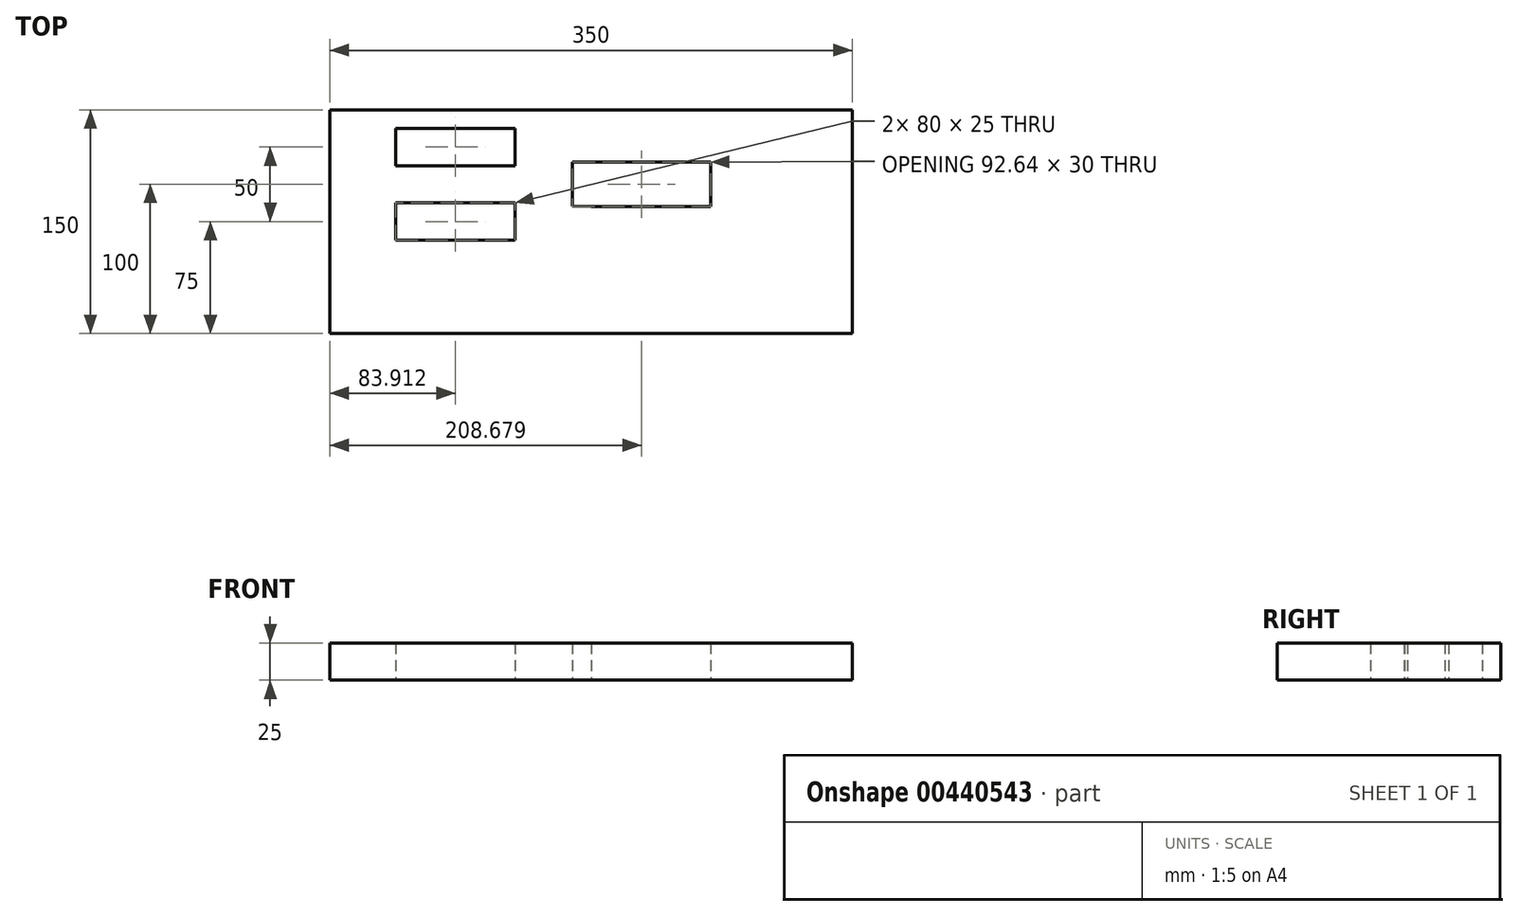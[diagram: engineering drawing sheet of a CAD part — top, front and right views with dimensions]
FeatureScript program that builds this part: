
annotation { "Feature Type Name" : "Feature", "Feature Type Description" : "" }
export const myFeature = defineFeature(function(context is Context, id is Id, definition is map)
    precondition{}
    {
        {
            var Q0;
            Q0=qCreatedBy(makeId("Top.planeOp"),FACE);
            var sketch = newSketch(context, id + "F0", { "sketchPlane" : qUnion([Q0])});
            skLineSegment(sketch, "E0.bottom", {"start": v(-175, 75) * mm, "end": v(175, 75) * mm});
            skLineSegment(sketch, "E0.top", {"start": v(-175, -75) * mm, "end": v(175, -75) * mm});
            skLineSegment(sketch, "E0.left", {"start": v(-175, 75) * mm, "end": v(-175, -75) * mm});
            skLineSegment(sketch, "E0.right", {"start": v(175, 75) * mm, "end": v(175, -75) * mm});
            skPoint(sketch, "E0.middle", {"position": v(0, 0) * mm});
            skLineSegment(sketch, "E1", {"start": v(-131.09, 62.5) * mm, "end": v(-51.09, 62.5) * mm});
            skLineSegment(sketch, "E2", {"start": v(-51.09, 37.5) * mm, "end": v(-131.09, 37.5) * mm});
            skLineSegment(sketch, "E3", {"start": v(-131.09, 12.5) * mm, "end": v(-51.09, 12.5) * mm});
            skLineSegment(sketch, "E4", {"start": v(-131.09, -12.5) * mm, "end": v(-51.09, -12.5) * mm});
            skLineSegment(sketch, "E5", {"start": v(-51.09, 62.5) * mm, "end": v(-51.09, 37.5) * mm});
            skLineSegment(sketch, "E6", {"start": v(-51.09, 12.5) * mm, "end": v(-51.09, -12.5) * mm});
            skLineSegment(sketch, "E7", {"start": v(-131.09, 12.5) * mm, "end": v(-131.09, -12.5) * mm});
            skLineSegment(sketch, "E8", {"start": v(-131.09, 37.5) * mm, "end": v(-131.09, 62.5) * mm});
            skLineSegment(sketch, "E9", {"start": v(0, -75) * mm, "end": v(80, -75) * mm});
            skLineSegment(sketch, "E10", {"start": v(80, 75) * mm, "end": v(0, 75) * mm});
            skLineSegment(sketch, "E11", {"start": v(0, 40) * mm, "end": v(80, 40) * mm});
            skLineSegment(sketch, "E12", {"start": v(80, 10) * mm, "end": v(0, 10) * mm});
            skLineSegment(sketch, "E13", {"start": v(80, 40) * mm, "end": v(80, 10) * mm});
            skLineSegment(sketch, "E14", {"start": v(0, 40) * mm, "end": v(-12.64, 40) * mm});
            skLineSegment(sketch, "E15", {"start": v(-12.64, 40) * mm, "end": v(-12.64, 10.44) * mm});
            skLineSegment(sketch, "E16", {"start": v(-12.64, 10.44) * mm, "end": v(0, 10) * mm});
            skSolve(sketch);
        }
        {
            var Q0;
            Q0=makeQuery(id+"F0.imprint","IMPRINT",FACE,{"disambiguationData":[TD([[makeQuery(id+"F0.imprint","IMPRINT",EDGE,{"derivedFrom":sQuery(id+"F0.wireOp",EDGE,"E0.bottom")}),-1.0]])]});
            extrude(context, id + "F1", {"entities" : qUnion([Q0]), "endBound" : BoundingType.SYMMETRIC, "depth" : 25 * mm});
        }
    });
